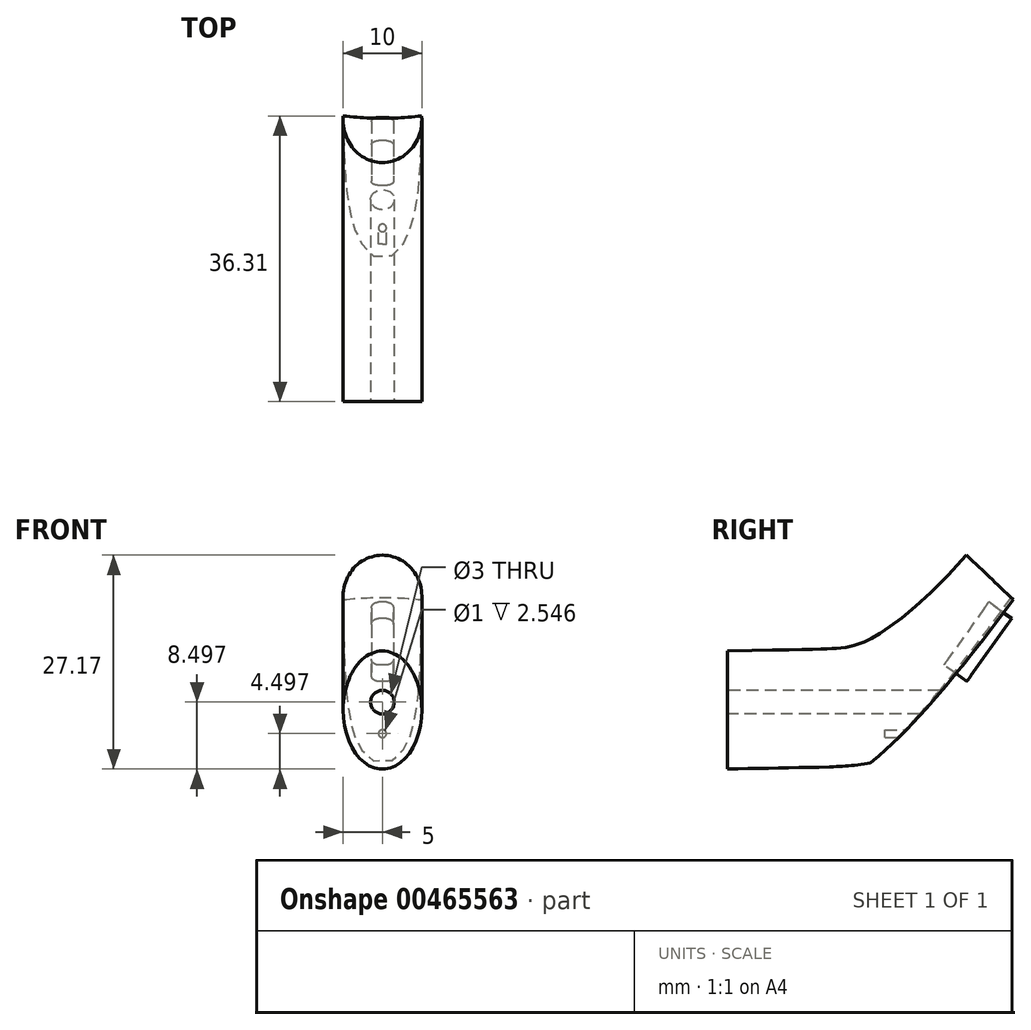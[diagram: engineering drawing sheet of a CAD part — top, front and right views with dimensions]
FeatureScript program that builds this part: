
annotation { "Feature Type Name" : "Feature", "Feature Type Description" : "" }
export const myFeature = defineFeature(function(context is Context, id is Id, definition is map)
    precondition{}
    {
        {
            var Q0;
            Q0=qCreatedBy(makeId("Front.planeOp"),FACE);
            var sketch = newSketch(context, id + "F0", { "sketchPlane" : qUnion([Q0])});
            skLineSegment(sketch, "E0", {"start": v(0, 31) * mm, "end": v(-11, 31) * mm});
            skLineSegment(sketch, "E1", {"start": v(-11, 31) * mm, "end": v(-11, 27) * mm});
            skLineSegment(sketch, "E2", {"start": v(-11, 27) * mm, "end": v(-20, 27) * mm});
            skLineSegment(sketch, "E3", {"start": v(-20, 27) * mm, "end": v(-20, 15) * mm});
            skLineSegment(sketch, "E4", {"start": v(-20, 15) * mm, "end": v(-23.79, 8.47) * mm});
            skLineSegment(sketch, "E5", {"start": v(-23.79, 8.47) * mm, "end": v(-25.24, 2) * mm});
            skLineSegment(sketch, "E6", {"start": v(-25.24, 2) * mm, "end": v(-26.3, 2) * mm});
            skLineSegment(sketch, "E7", {"start": v(-26.3, 2) * mm, "end": v(-26.3, 1) * mm});
            skLineSegment(sketch, "E8", {"start": v(-26.3, 1) * mm, "end": v(0, 1) * mm});
            skLineSegment(sketch, "E9", {"start": v(0, 1) * mm, "end": v(0, 31) * mm});
            skLineSegment(sketch, "E10.MirrorCS", {"start": v(0, 31) * mm, "end": v(11, 31) * mm});
            skLineSegment(sketch, "E11.MirrorCS", {"start": v(11, 31) * mm, "end": v(11, 27) * mm});
            skLineSegment(sketch, "E12.MirrorCS", {"start": v(11, 27) * mm, "end": v(20, 27) * mm});
            skLineSegment(sketch, "E13.MirrorCS", {"start": v(20, 27) * mm, "end": v(20, 15) * mm});
            skLineSegment(sketch, "E14.MirrorCS", {"start": v(20, 15) * mm, "end": v(23.79, 8.47) * mm});
            skLineSegment(sketch, "E15.MirrorCS", {"start": v(23.79, 8.47) * mm, "end": v(25.24, 2) * mm});
            skLineSegment(sketch, "E16.MirrorCS", {"start": v(26.3, 2) * mm, "end": v(26.3, 1) * mm});
            skLineSegment(sketch, "E17.MirrorCS", {"start": v(26.3, 1) * mm, "end": v(0, 1) * mm});
            skLineSegment(sketch, "E18.MirrorCS", {"start": v(25.24, 2) * mm, "end": v(26.3, 2) * mm});
            skPoint(sketch, "E19", {"position": v(0, 1) * mm});
            skSolve(sketch);
        }
        {
            var Q0;
            Q0=qCreatedBy(makeId("Front.planeOp"),FACE);
            var sketch = newSketch(context, id + "F1", { "sketchPlane" : qUnion([Q0])});
            skArc(sketch, "E20", {"start": v(11, 43.93) * mm, "mid": v(6.28, 48.38) * mm, "end": v(0, 50) * mm});
            skFitSpline(sketch, "E21", {"points": [v(11, 43.93) * mm, v(31, 15.5) * mm, v(47.5, 0) * mm], "startDerivative": vector(35.28, -56.02) * mm, "endDerivative": vector(42.1, -23.63) * mm});
            skLineSegment(sketch, "E22", {"start": v(0, 0) * mm, "end": v(0, 58.78) * mm, "construction": true});
            skArc(sketch, "E23.1", {"start": v(9.73, 43.13) * mm, "mid": v(5.56, 47.07) * mm, "end": v(0, 48.5) * mm});
            skLineSegment(sketch, "E24", {"start": v(0, 48.5) * mm, "end": v(0, 50) * mm});
            skLineSegment(sketch, "E25", {"start": v(47.5, 0) * mm, "end": v(44, 0) * mm});
            skLineSegment(sketch, "E26", {"start": v(41.81, 1) * mm, "end": v(44, 1) * mm});
            skLineSegment(sketch, "E27", {"start": v(44, 1) * mm, "end": v(44, 0) * mm});
            skLineSegment(sketch, "E28", {"start": v(41.81, 1) * mm, "end": v(14.28, 21.6) * mm});
            skLineSegment(sketch, "E29", {"start": v(14.28, 21.6) * mm, "end": v(9.73, 43.13) * mm});
            skSolve(sketch);
        }
        {
            var Q0;
            Q0=qSketchRegion(id+"F1",true);
            var Q1;
            Q1=sQuery(id+"F1.wireOp",EDGE,"E22");
            revolve(context, id + "F2", {"entities" : qUnion([Q0]), "axis" : qUnion([Q1]), "revolveType" : RevolveType.FULL});
        }
        {
            var Q0;
            Q0=qCreatedBy(makeId("Right.planeOp"),FACE);
            var sketch = newSketch(context, id + "F3", { "sketchPlane" : qUnion([Q0])});
            skLineSegment(sketch, "E30", {"start": v(-16.56, 37) * mm, "end": v(-14.55, 37) * mm});
            skLineSegment(sketch, "E31", {"start": v(-14.55, 37) * mm, "end": v(-25.44, 21.72) * mm});
            skLineSegment(sketch, "E32", {"start": v(-25.44, 21.72) * mm, "end": v(-28.94, 21.72) * mm});
            skLineSegment(sketch, "E33", {"start": v(-28.94, 21.72) * mm, "end": v(-16.56, 37) * mm});
            skSolve(sketch);
        }
        {
            var Q0;
            Q0=sQuery(id+"F3.wireOp",EDGE,"E31");
            cPlane(context, id + "F4", {"entities" : qUnion([Q0]), "cplaneType" : CPlaneType.LINE_ANGLE, "offset" : 25 * mm, "angle" : 90 * degree, "width" : 150 * mm, "height" : 150 * mm});
        }
        {
            var Q0;
            Q0=qCreatedBy(id+"F4.planeOp",FACE);
            var sketch = newSketch(context, id + "F5", { "sketchPlane" : qUnion([Q0])});
            skLineSegment(sketch, "E34.bottom", {"start": v(-1.5, 4) * mm, "end": v(-1.5, -4) * mm, "construction": true});
            skLineSegment(sketch, "E34.top", {"start": v(1.5, 4) * mm, "end": v(1.5, -4) * mm, "construction": true});
            skLineSegment(sketch, "E34.left", {"start": v(-0.5, 5) * mm, "end": v(0.5, 5) * mm, "construction": true});
            skLineSegment(sketch, "E34.right", {"start": v(-0.5, -5) * mm, "end": v(0.5, -5) * mm, "construction": true});
            skPoint(sketch, "E34.middle", {"position": v(0, 0) * mm});
            skPoint(sketch, "E34.middle.positionSnap0", {"position": v(-1.5, 0) * mm});
            skPoint(sketch, "E34.middle.positionSnap1", {"position": v(0, 4.6) * mm});
            skPoint(sketch, "E34.cornerSnap0", {"position": v(-1.5, -0.4) * mm});
            skPoint(sketch, "E34.cornerSnap1", {"position": v(0, 5) * mm});
            skPoint(sketch, "E34.centerSnap0", {"position": v(-1.5, 0) * mm});
            skPoint(sketch, "E34.centerSnap1", {"position": v(0, 4.6) * mm});
            skPoint(sketch, "E35.visualSharp", {"position": v(-1.5, -5) * mm});
            skArc(sketch, "E35.filletArc", {"start": v(-1.5, -4) * mm, "mid": v(-1.2, -4.7) * mm, "end": v(-0.5, -5) * mm, "construction": true});
            skPoint(sketch, "E36.visualSharp", {"position": v(1.5, -5) * mm});
            skArc(sketch, "E36.filletArc", {"start": v(0.5, -5) * mm, "mid": v(1.2, -4.7) * mm, "end": v(1.5, -4) * mm, "construction": true});
            skPoint(sketch, "E37.visualSharp", {"position": v(1.5, 5) * mm});
            skArc(sketch, "E37.filletArc", {"start": v(1.5, 4) * mm, "mid": v(1.2, 4.7) * mm, "end": v(0.5, 5) * mm, "construction": true});
            skPoint(sketch, "E38.visualSharp", {"position": v(-1.5, 5) * mm});
            skArc(sketch, "E38.filletArc", {"start": v(-0.5, 5) * mm, "mid": v(-1.2, 4.7) * mm, "end": v(-1.5, 4) * mm, "construction": true});
            skArc(sketch, "E39.0", {"start": v(1.4, 4) * mm, "mid": v(1.14, 4.64) * mm, "end": v(0.5, 4.9) * mm});
            skLineSegment(sketch, "E39.1", {"start": v(-0.5, 4.9) * mm, "end": v(0.5, 4.9) * mm});
            skLineSegment(sketch, "E39.2", {"start": v(1.4, 4) * mm, "end": v(1.4, -4) * mm});
            skArc(sketch, "E39.3", {"start": v(-0.5, 4.9) * mm, "mid": v(-1.14, 4.64) * mm, "end": v(-1.4, 4) * mm});
            skArc(sketch, "E39.4", {"start": v(0.5, -4.9) * mm, "mid": v(1.14, -4.64) * mm, "end": v(1.4, -4) * mm});
            skLineSegment(sketch, "E39.5", {"start": v(-0.5, -4.9) * mm, "end": v(0.5, -4.9) * mm});
            skArc(sketch, "E39.6", {"start": v(-1.4, -4) * mm, "mid": v(-1.14, -4.64) * mm, "end": v(-0.5, -4.9) * mm});
            skLineSegment(sketch, "E39.7", {"start": v(-1.4, 4) * mm, "end": v(-1.4, -4) * mm});
            skSolve(sketch);
        }
        {
            var Q0;
            Q0=qSketchRegion(id+"F5",true);
            extrude(context, id + "F6", {"entities" : qUnion([Q0]), "depth" : 1.1 * mm, "hasSecondDirection" : true, "secondDirectionOppositeDirection" : true, "secondDirectionDepth" : 2.5 * mm});
        }
        {
            var Q0;
            Q0=qCreatedBy(makeId("Right.planeOp"),FACE);
            var sketch = newSketch(context, id + "F7", { "sketchPlane" : qUnion([Q0])});
            skFitSpline(sketch, "E40", {"points": [v(-59.5, 11.06) * mm, v(-44.5, 11.48) * mm, v(-23.7, 25.56) * mm], "startDerivative": vector(77.91, 1.88) * mm, "endDerivative": vector(61.7, 68.08) * mm});
            skSolve(sketch);
        }
        {
            var Q0;
            Q0=qCreatedBy(makeId("Front.planeOp"),FACE);
            var Q1;
            Q1=sQuery(id+"F7.wireOp",VERTEX,"E40.0.internal");
            cPlane(context, id + "F8", {"entities" : qUnion([Q0, Q1]), "cplaneType" : CPlaneType.PLANE_POINT, "offset" : 25 * mm, "width" : 150 * mm, "height" : 150 * mm});
        }
        {
            var Q0;
            Q0=qCreatedBy(id+"F8.planeOp",FACE);
            var sketch = newSketch(context, id + "F9", { "sketchPlane" : qUnion([Q0])});
            skCircle(sketch, "E41", {"center": v(0, 11.06) * mm, "radius": 4 * mm, "construction": true});
            skEllipse(sketch, "E42", {"center": v(0, 11.06) * mm, "majorRadius": 7.5 * mm, "minorRadius": 5 * mm, "majorAxis": v(0, 1)});
            skSolve(sketch);
        }
        {
            var Q0;
            Q0=makeQuery(id+"F9.imprint","IMPRINT",FACE,{"disambiguationData":[TD([[makeQuery(id+"F9.imprint","IMPRINT",EDGE,{"derivedFrom":sQuery(id+"F9.wireOp",EDGE,"E42")}),1.0]])]});
            var Q1;
            Q1=sQuery(id+"F7.wireOp",EDGE,"E40");
            sweep(context, id + "F10", {"profiles" : qUnion([Q0]), "path" : qUnion([Q1])});
        }
        {
            var Q0;
            Q0=makeQuery(id+"F2.opRevolve","SWEPT_BODY",BODY,{"disambiguationData":[OSD([sQuery(id+"F1.wireOp",EDGE,"E20"),sQuery(id+"F1.wireOp",EDGE,"E21"),sQuery(id+"F1.wireOp",EDGE,"E23.0"),sQuery(id+"F1.wireOp",EDGE,"E23.1"),sQuery(id+"F1.wireOp",EDGE,"E24"),sQuery(id+"F1.wireOp",EDGE,"XYFtmsl9-VjrF-HnEM-VMgo-AzE1E2IRDEMY"),sQuery(id+"F1.wireOp",EDGE,"NrGoaARt-aIj9-E4UK-RGhr-GKT9ADPdkPlm"),sQuery(id+"F1.wireOp",EDGE,"dcc3acc6-d380-4a49-83e3-f377f92320a5.trimOffspring"),sQuery(id+"F1.wireOp",EDGE,"E25"),sQuery(id+"F1.wireOp",EDGE,"mI7R0eBA-hv5c-FRNt-wdh4-h6GYI6LebP1T"),sQuery(id+"F1.wireOp",EDGE,"E26"),sQuery(id+"F1.wireOp",EDGE,"E27")])]});
            var Q1;
            Q1=makeQuery(id+"F10.opSweep","SWEPT_BODY",BODY,{"disambiguationData":[OSD([sQuery(id+"F7.wireOp",EDGE,"E40"),sQuery(id+"F9.wireOp",EDGE,"E41")])]});
            booleanBodies(context, id + "F11", {"operationType" : BooleanOperationType.SUBTRACTION, "tools" : qUnion([Q0]), "targets" : qUnion([Q1])});
        }
        {
            var Q0;
            Q0=makeQuery(id+"F9.imprint","IMPRINT",FACE,{"disambiguationData":[TD([[makeQuery(id+"F9.imprint","IMPRINT",EDGE,{"derivedFrom":sQuery(id+"F9.wireOp",EDGE,"E42")}),1.0]])]});
            var sketch = newSketch(context, id + "F12", { "sketchPlane" : qUnion([Q0])});
            skCircle(sketch, "E43", {"center": v(0, 12.06) * mm, "radius": 1.5 * mm});
            skSolve(sketch);
        }
        {
            var Q0;
            Q0=makeQuery(id+"F12.imprint","IMPRINT",FACE,{"disambiguationData":[TD([[makeQuery(id+"F12.imprint","IMPRINT",EDGE,{"derivedFrom":sQuery(id+"F12.wireOp",EDGE,"E43")}),1.0]])]});
            extrude(context, id + "F13", {"entities" : qUnion([Q0]), "operationType" : NewBodyOperationType.REMOVE, "oppositeDirection" : true, "depth" : 27.4 * mm, "offsetDistance" : 25 * mm});
        }
        {
            var Q0;
            Q0=qCreatedBy(makeId("Right.planeOp"),FACE);
            var sketch = newSketch(context, id + "F14", { "sketchPlane" : qUnion([Q0])});
            skLineSegment(sketch, "E44", {"start": v(-24.37, 0.84) * mm, "end": v(-35.64, 7.24) * mm});
            skLineSegment(sketch, "E45", {"start": v(-35.64, 7.24) * mm, "end": v(-24.6, 16.1) * mm});
            skLineSegment(sketch, "E46", {"start": v(-24.6, 16.1) * mm, "end": v(-19.48, 9.73) * mm});
            skLineSegment(sketch, "E47", {"start": v(-19.48, 9.73) * mm, "end": v(-24.37, 0.84) * mm});
            skSolve(sketch);
        }
        {
            var Q0;
            Q0=makeQuery(id+"F14.imprint","IMPRINT",FACE,{"disambiguationData":[TD([[makeQuery(id+"F14.imprint","IMPRINT",EDGE,{"derivedFrom":sQuery(id+"F14.wireOp",EDGE,"E44")}),-1.0]])]});
            extrude(context, id + "F15", {"entities" : qUnion([Q0]), "operationType" : NewBodyOperationType.REMOVE, "oppositeDirection" : true, "depth" : 25 * mm, "offsetDistance" : 25 * mm, "hasSecondDirection" : true, "secondDirectionOppositeDirection" : false, "secondDirectionDepth" : 25 * mm});
        }
        {
            var Q0;
            Q0=makeQuery(id+"F9.imprint","IMPRINT",FACE,{"disambiguationData":[TD([[makeQuery(id+"F9.imprint","IMPRINT",EDGE,{"derivedFrom":sQuery(id+"F9.wireOp",EDGE,"E42")}),1.0]])]});
            cPlane(context, id + "F16", {"entities" : qUnion([Q0]), "cplaneType" : CPlaneType.OFFSET, "offset" : 25 * mm, "oppositeDirection" : true, "width" : 150 * mm, "height" : 150 * mm});
        }
        {
            var Q0;
            Q0=qCreatedBy(id+"F16.planeOp",FACE);
            var sketch = newSketch(context, id + "F17", { "sketchPlane" : qUnion([Q0])});
            skCircle(sketch, "E48", {"center": v(0, 8.06) * mm, "radius": 0.5 * mm});
            skSolve(sketch);
        }
        {
            var Q0;
            Q0=makeQuery(id+"F17.imprint","IMPRINT",FACE,{"disambiguationData":[TD([[makeQuery(id+"F17.imprint","IMPRINT",EDGE,{"derivedFrom":sQuery(id+"F17.wireOp",EDGE,"E48")}),1.0]])]});
            extrude(context, id + "F18", {"entities" : qUnion([Q0]), "operationType" : NewBodyOperationType.REMOVE, "depth" : 5 * mm, "offsetDistance" : 25 * mm});
        }
    });
